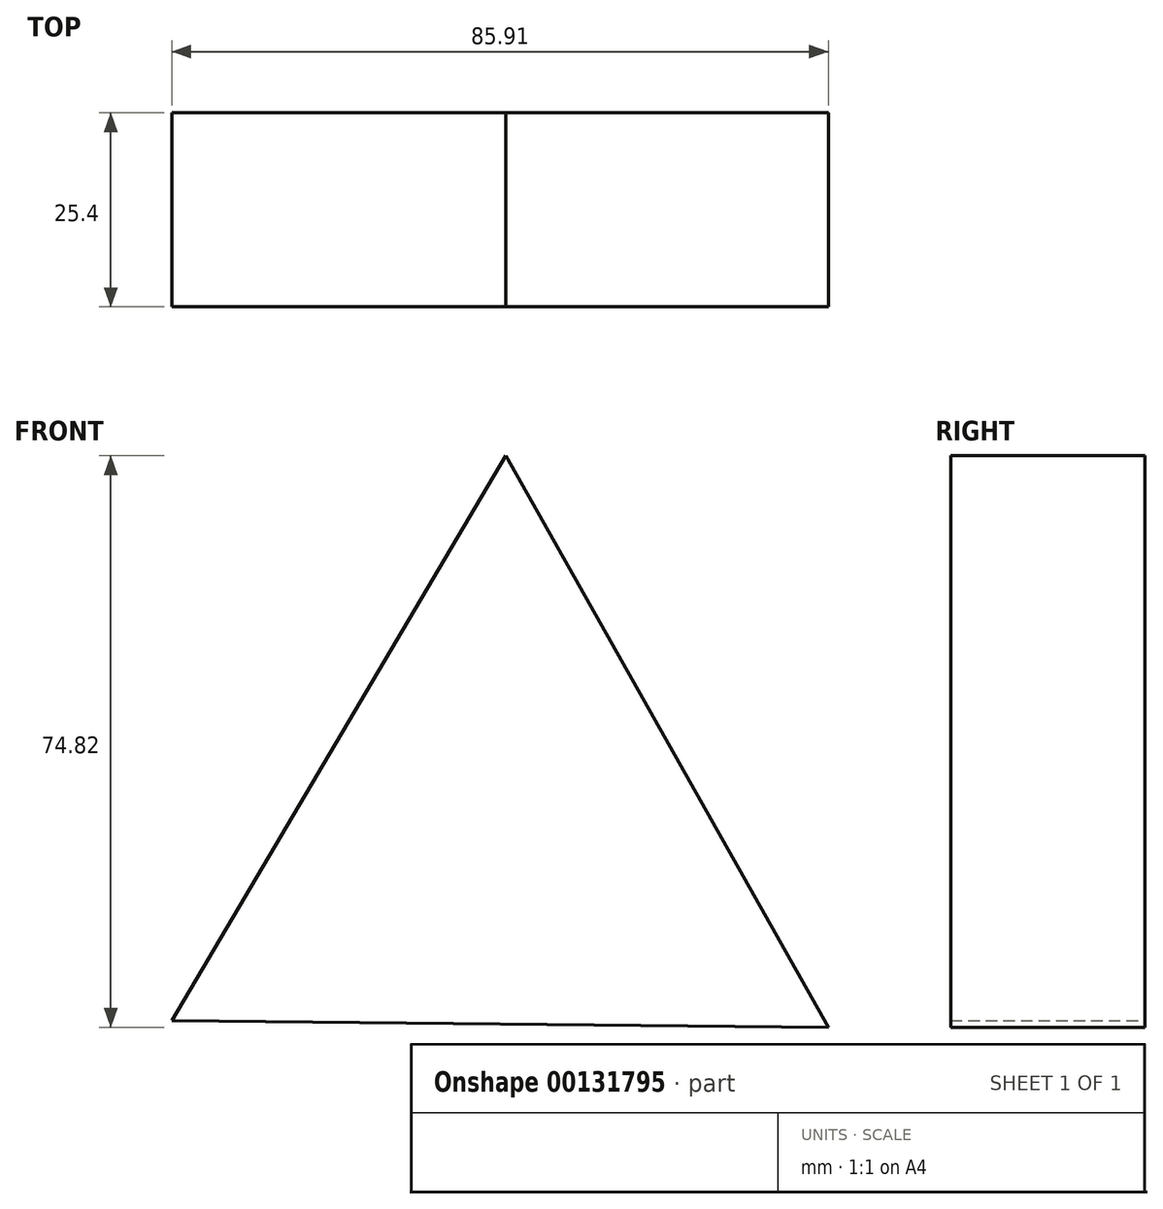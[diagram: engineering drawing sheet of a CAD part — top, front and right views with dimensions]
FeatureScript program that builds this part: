
annotation { "Feature Type Name" : "Feature", "Feature Type Description" : "" }
export const myFeature = defineFeature(function(context is Context, id is Id, definition is map)
    precondition{}
    {
        {
            var Q0;
            Q0=qCreatedBy(makeId("Front.planeOp"),FACE);
            var sketch = newSketch(context, id + "F0", { "sketchPlane" : qUnion([Q0])});
            skCircle(sketch, "E0.cCircle", {"center": v(0, -10.22) * mm, "radius": 24.8 * mm, "construction": true});
            skLineSegment(sketch, "E0.0", {"start": v(42.71, -35.44) * mm, "end": v(-43.2, -34.6) * mm});
            skLineSegment(sketch, "E0.1", {"start": v(-43.2, -34.6) * mm, "end": v(0.49, 39.38) * mm});
            skLineSegment(sketch, "E0.2", {"start": v(0.49, 39.38) * mm, "end": v(42.71, -35.44) * mm});
            skPoint(sketch, "E0.0.midPoint", {"position": v(-0.24, -35.02) * mm});
            skSolve(sketch);
        }
        {
            var Q0;
            Q0 = qSketchRegion(id + "F0", true);
            extrude(context, id + "F1", {"entities" : qUnion([Q0]), "depth" : 25.4 * mm});
        }
    });
